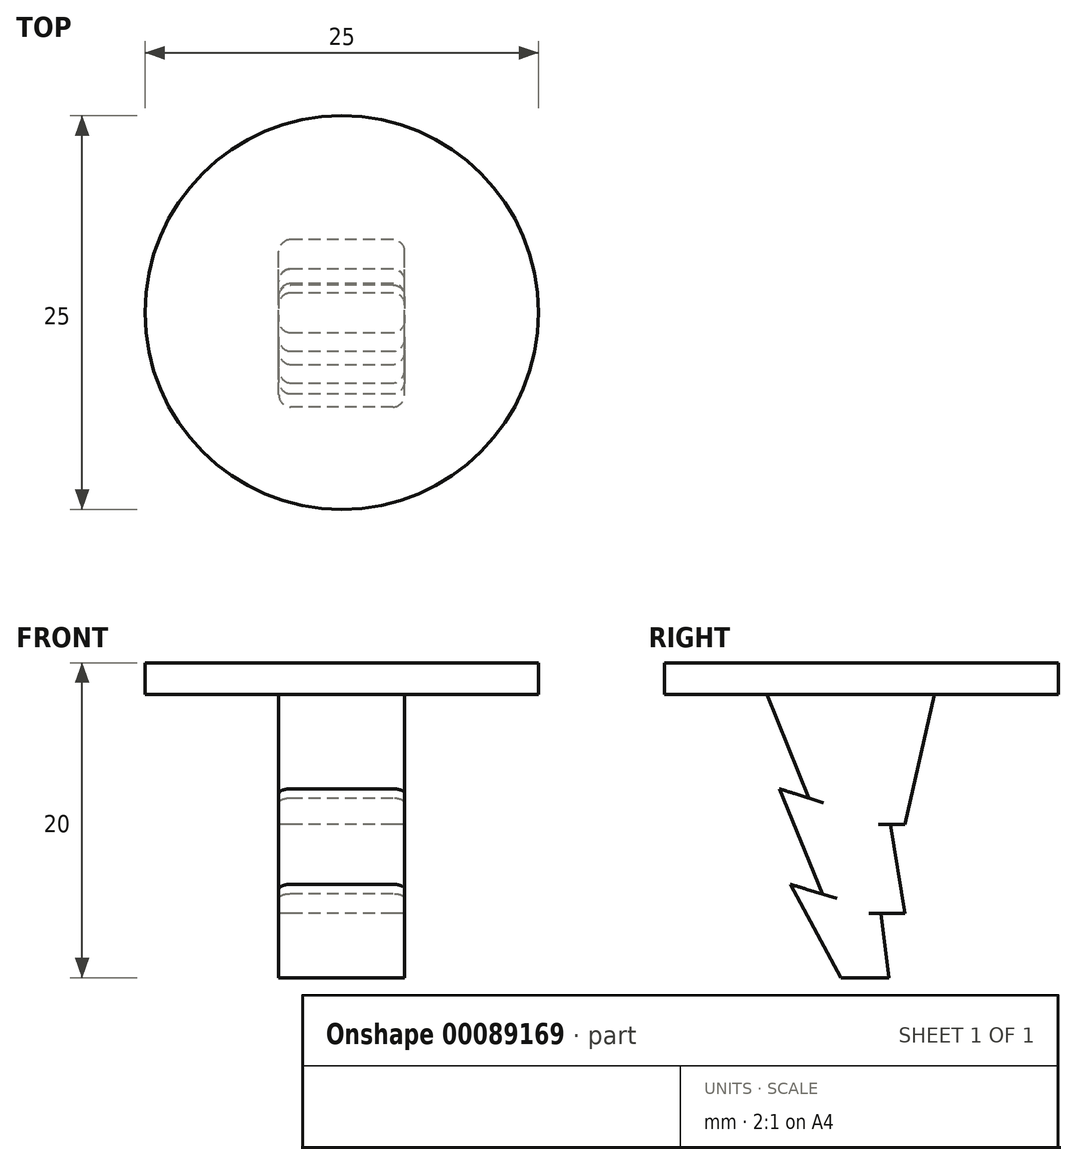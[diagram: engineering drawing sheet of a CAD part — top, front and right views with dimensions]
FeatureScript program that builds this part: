
annotation { "Feature Type Name" : "Feature", "Feature Type Description" : "" }
export const myFeature = defineFeature(function(context is Context, id is Id, definition is map)
    precondition{}
    {
        {
            var Q0;
            Q0=qCreatedBy(makeId("Top.planeOp"),FACE);
            var sketch = newSketch(context, id + "F0", { "sketchPlane" : qUnion([Q0])});
            skCircle(sketch, "E0", {"center": v(0, 0) * mm, "radius": 12.5 * mm});
            skSolve(sketch);
        }
        {
            var Q0;
            Q0=makeQuery(id+"F0.imprint","IMPRINT",FACE,{"disambiguationData":[TD([[makeQuery(id+"F0.imprint","IMPRINT",EDGE,{"derivedFrom":sQuery(id+"F0.wireOp",EDGE,"E0")}),1.0]])]});
            extrude(context, id + "F1", {"entities" : qUnion([Q0]), "depth" : 2 * mm});
        }
        {
            var Q0;
            Q0=qCreatedBy(makeId("Right.planeOp"),FACE);
            var sketch = newSketch(context, id + "F2", { "sketchPlane" : qUnion([Q0])});
            skPoint(sketch, "E1", {"position": v(-6, 0) * mm});
            skPoint(sketch, "E2", {"position": v(6, 0) * mm});
            skLineSegment(sketch, "E3", {"start": v(0, 0) * mm, "end": v(0, -18) * mm, "construction": true});
            skPoint(sketch, "E4.orphan", {"position": v(4.63, 0) * mm});
            skPoint(sketch, "E5.start.orphan", {"position": v(-3.45, 0) * mm});
            skLineSegment(sketch, "E6", {"start": v(-6, 0) * mm, "end": v(-3.32, -6.6) * mm});
            skLineSegment(sketch, "E7", {"start": v(-3.32, -6.6) * mm, "end": v(-5.19, -6) * mm});
            skLineSegment(sketch, "E8", {"start": v(-5.19, -6) * mm, "end": v(-2.48, -12.69) * mm});
            skLineSegment(sketch, "E9", {"start": v(-2.48, -12.69) * mm, "end": v(-4.5, -12.07) * mm});
            skLineSegment(sketch, "E10", {"start": v(-4.5, -12.07) * mm, "end": v(-1.3, -18) * mm});
            skLineSegment(sketch, "E11", {"start": v(1.25, -13.9) * mm, "end": v(2.77, -13.9) * mm});
            skLineSegment(sketch, "E12", {"start": v(1.84, -8.25) * mm, "end": v(2.75, -8.25) * mm});
            skLineSegment(sketch, "E13", {"start": v(2.75, -8.25) * mm, "end": v(4.63, 0) * mm});
            skPoint(sketch, "E14.orphan", {"position": v(1.03, -18) * mm});
            skLineSegment(sketch, "E15", {"start": v(0, -18) * mm, "end": v(-1.3, -18) * mm});
            skLineSegment(sketch, "E16", {"start": v(0, -18) * mm, "end": v(1.75, -18) * mm});
            skLineSegment(sketch, "E17", {"start": v(1.75, -18) * mm, "end": v(1.25, -13.9) * mm});
            skLineSegment(sketch, "E18", {"start": v(1.84, -8.25) * mm, "end": v(2.77, -13.9) * mm});
            skLineSegment(sketch, "E19", {"start": v(-6, 0) * mm, "end": v(4.63, 0) * mm});
            skSolve(sketch);
        }
        {
            var Q0;
            Q0=makeQuery(id+"F2.imprint","IMPRINT",FACE,{"disambiguationData":[TD([[makeQuery(id+"F2.imprint","IMPRINT",EDGE,{"derivedFrom":sQuery(id+"F2.wireOp",EDGE,"E6")}),1.0]])]});
            extrude(context, id + "F3", {"entities" : qUnion([Q0]), "operationType" : NewBodyOperationType.ADD, "depth" : 4 * mm, "hasSecondDirection" : true, "secondDirectionOppositeDirection" : true, "secondDirectionDepth" : 4 * mm});
        }
        {
            var Q0;
            Q0=makeQuery(id+"F3.opExtrude","CAP_EDGE",EDGE,{"disambiguationData":[OSD([sQuery(id+"F2.wireOp",EDGE,"E13")])],"isStart":true});
            var Q1;
            Q1=makeQuery(id+"F3.opExtrude","CAP_EDGE",EDGE,{"disambiguationData":[OSD([sQuery(id+"F2.wireOp",EDGE,"E6")])],"isStart":true});
            var Q2;
            Q2=makeQuery(id+"F3.opExtrude","CAP_EDGE",EDGE,{"disambiguationData":[OSD([sQuery(id+"F2.wireOp",EDGE,"E18")])],"isStart":true});
            var Q3;
            Q3=makeQuery(id+"F3.opExtrude","CAP_EDGE",EDGE,{"disambiguationData":[OSD([sQuery(id+"F2.wireOp",EDGE,"E8")])],"isStart":true});
            var Q4;
            Q4=makeQuery(id+"F3.opExtrude","CAP_EDGE",EDGE,{"disambiguationData":[OSD([sQuery(id+"F2.wireOp",EDGE,"E17")])],"isStart":true});
            var Q5;
            Q5=makeQuery(id+"F3.opExtrude","CAP_EDGE",EDGE,{"disambiguationData":[OSD([sQuery(id+"F2.wireOp",EDGE,"E10")])],"isStart":true});
            var Q6;
            Q6=makeQuery(id+"F3.opExtrude","CAP_EDGE",EDGE,{"disambiguationData":[OSD([sQuery(id+"F2.wireOp",EDGE,"E13")])],"isStart":false});
            var Q7;
            Q7=makeQuery(id+"F3.opExtrude","CAP_EDGE",EDGE,{"disambiguationData":[OSD([sQuery(id+"F2.wireOp",EDGE,"E18")])],"isStart":false});
            var Q8;
            Q8=makeQuery(id+"F3.opExtrude","CAP_EDGE",EDGE,{"disambiguationData":[OSD([sQuery(id+"F2.wireOp",EDGE,"E10")])],"isStart":false});
            var Q9;
            Q9=makeQuery(id+"F3.opExtrude","CAP_EDGE",EDGE,{"disambiguationData":[OSD([sQuery(id+"F2.wireOp",EDGE,"E17")])],"isStart":false});
            var Q10;
            Q10=makeQuery(id+"F3.opExtrude","CAP_EDGE",EDGE,{"disambiguationData":[OSD([sQuery(id+"F2.wireOp",EDGE,"E8")])],"isStart":false});
            var Q11;
            Q11=makeQuery(id+"F3.opExtrude","CAP_EDGE",EDGE,{"disambiguationData":[OSD([sQuery(id+"F2.wireOp",EDGE,"E6")])],"isStart":false});
            fillet(context, id + "F4", {"entities" : qUnion([Q0, Q1, Q2, Q3, Q4, Q5, Q6, Q7, Q8, Q9, Q10, Q11]), "radius" : .75 * mm, "tangentPropagation" : true, "allowEdgeOverflow" : false});
        }
    });
